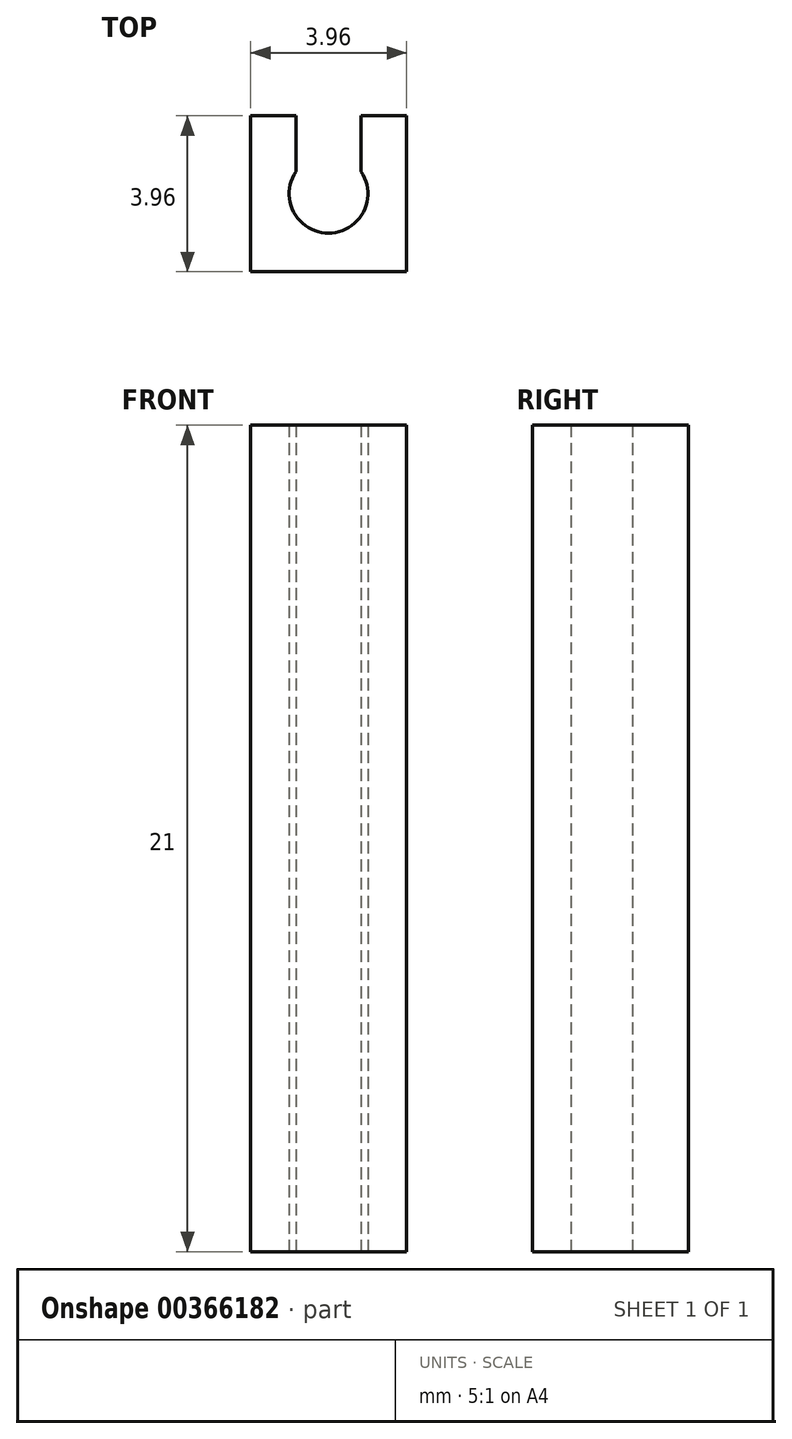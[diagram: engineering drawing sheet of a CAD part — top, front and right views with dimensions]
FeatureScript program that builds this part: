
annotation { "Feature Type Name" : "Feature", "Feature Type Description" : "" }
export const myFeature = defineFeature(function(context is Context, id is Id, definition is map)
    precondition{}
    {
        {
            var Q0;
            Q0=qCreatedBy(makeId("Top.planeOp"),FACE);
            var sketch = newSketch(context, id + "F0", { "sketchPlane" : qUnion([Q0])});
            skCircle(sketch, "E0", {"center": v(0, 0) * mm, "radius": 2.8 * mm, "construction": true});
            skLineSegment(sketch, "E1.bottom", {"start": v(1.98, 1.98) * mm, "end": v(0.83, 1.98) * mm});
            skLineSegment(sketch, "E1.top", {"start": v(1.98, -1.98) * mm, "end": v(-1.98, -1.98) * mm});
            skLineSegment(sketch, "E1.left", {"start": v(1.98, 1.98) * mm, "end": v(1.98, -1.98) * mm});
            skLineSegment(sketch, "E1.right", {"start": v(-1.98, 1.98) * mm, "end": v(-1.98, -1.98) * mm});
            skArc(sketch, "E2", {"start": v(-0.83, 0.56) * mm, "mid": v(0, -1) * mm, "end": v(0.83, 0.56) * mm});
            skLineSegment(sketch, "E3", {"start": v(-0.83, 0.56) * mm, "end": v(-0.83, 1.98) * mm});
            skLineSegment(sketch, "E4.MirrorCS", {"start": v(0.83, 0.56) * mm, "end": v(0.83, 1.98) * mm});
            skLineSegment(sketch, "E5.trimOffspring", {"start": v(-0.83, 1.98) * mm, "end": v(-1.98, 1.98) * mm});
            skCircle(sketch, "E6", {"center": v(0, 0) * mm, "radius": 2.5 * mm, "construction": true});
            skSolve(sketch);
        }
        {
            var Q0;
            Q0 = qSketchRegion(id + "F0", true);
            extrude(context, id + "F1", {"entities" : qUnion([Q0]), "depth" : 21 * mm});
        }
    });
